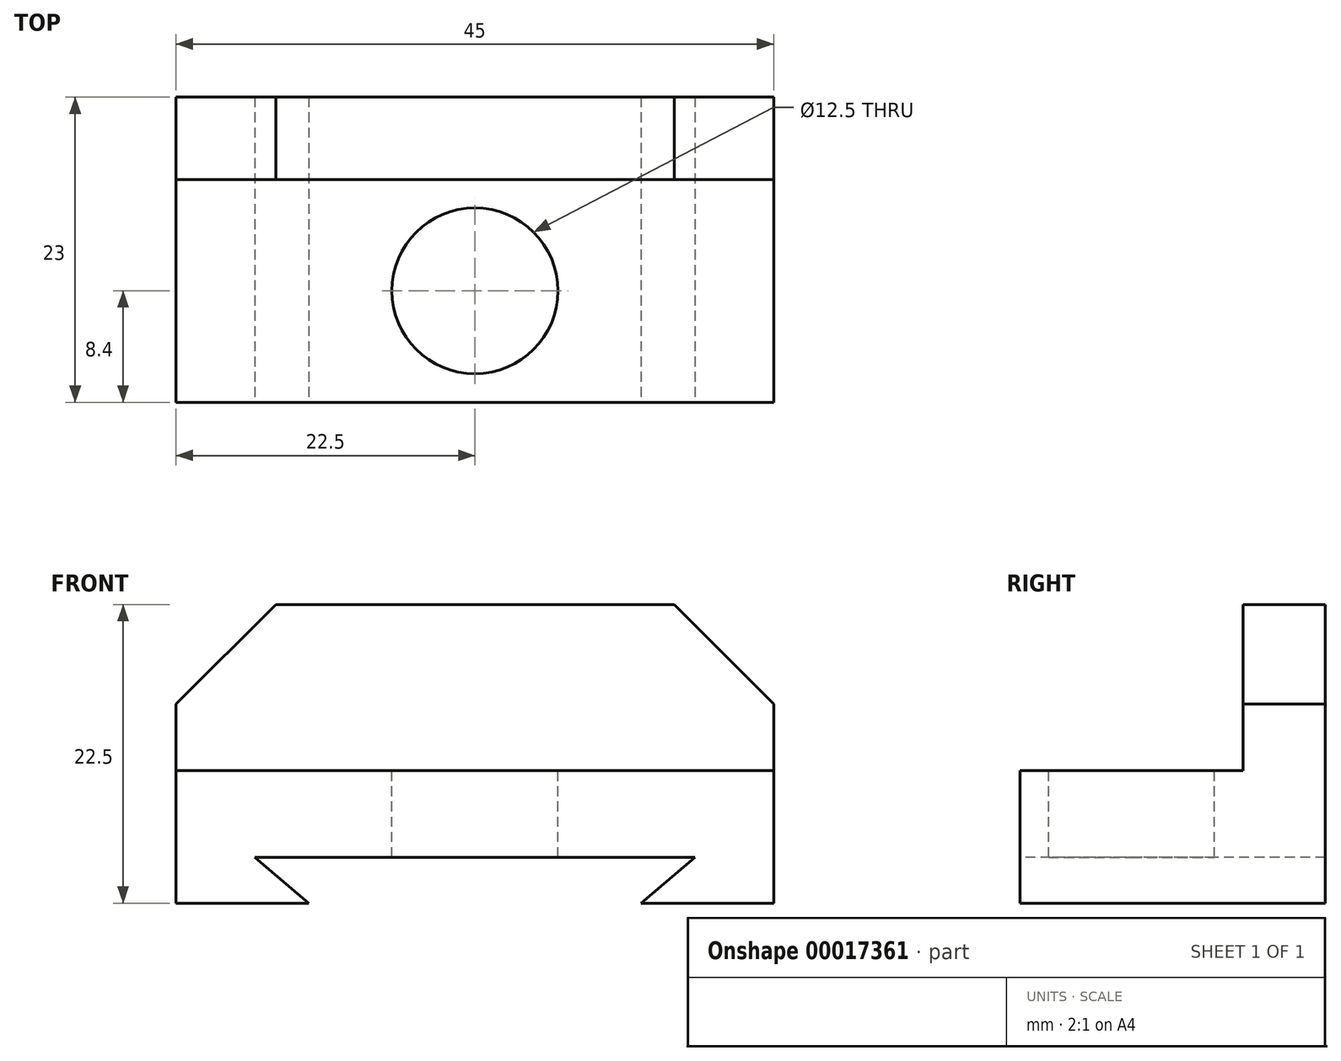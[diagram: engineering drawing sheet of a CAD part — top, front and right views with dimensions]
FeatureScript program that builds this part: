
annotation { "Feature Type Name" : "Feature", "Feature Type Description" : "" }
export const myFeature = defineFeature(function(context is Context, id is Id, definition is map)
    precondition{}
    {
        {
            var Q0;
            Q0=qCreatedBy(makeId("Front.planeOp"),FACE);
            var sketch = newSketch(context, id + "F0", { "sketchPlane" : qUnion([Q0])});
            skLineSegment(sketch, "E0", {"start": v(-24.57, -27) * mm, "end": v(-14.57, -27) * mm});
            skLineSegment(sketch, "E1", {"start": v(10.43, -27) * mm, "end": v(20.43, -27) * mm});
            skLineSegment(sketch, "E2", {"start": v(20.43, -27) * mm, "end": v(20.43, -17) * mm});
            skLineSegment(sketch, "E3", {"start": v(-24.57, -27) * mm, "end": v(-24.57, -17) * mm});
            skLineSegment(sketch, "E4", {"start": v(-24.57, -17) * mm, "end": v(20.43, -17) * mm});
            skLineSegment(sketch, "E5", {"start": v(-14.57, -27) * mm, "end": v(-18.64, -23.54) * mm});
            skLineSegment(sketch, "E6", {"start": v(10.43, -27) * mm, "end": v(14.5, -23.54) * mm});
            skLineSegment(sketch, "E7", {"start": v(14.5, -23.54) * mm, "end": v(-18.64, -23.54) * mm});
            skSolve(sketch);
        }
        {
            var Q0;
            Q0=makeQuery(id+"F0.imprint","IMPRINT",FACE,{"disambiguationData":[TD([[makeQuery(id+"F0.imprint","IMPRINT",EDGE,{"derivedFrom":sQuery(id+"F0.wireOp",EDGE,"E0")}),1.0]])]});
            extrude(context, id + "F1", {"entities" : qUnion([Q0]), "oppositeDirection" : true, "depth" : 23 * mm});
        }
        {
            var Q0;
            Q0=makeQuery(id+"F1.opExtrude","SWEPT_FACE",FACE,{"disambiguationData":[OSD([sQuery(id+"F0.wireOp",EDGE,"E4")])]});
            var sketch = newSketch(context, id + "F2", { "sketchPlane" : qUnion([Q0])});
            skLineSegment(sketch, "E8.bottom", {"start": v(-24.57, 23) * mm, "end": v(20.43, 23) * mm});
            skLineSegment(sketch, "E8.top", {"start": v(-24.57, 16.8) * mm, "end": v(20.43, 16.8) * mm});
            skLineSegment(sketch, "E8.left", {"start": v(-24.57, 23) * mm, "end": v(-24.57, 16.8) * mm});
            skLineSegment(sketch, "E8.right", {"start": v(20.43, 23) * mm, "end": v(20.43, 16.8) * mm});
            skSolve(sketch);
        }
        {
            var Q0;
            Q0=makeQuery(id+"F2.imprint","IMPRINT",FACE,{"disambiguationData":[TD([[makeQuery(id+"F2.imprint","IMPRINT",EDGE,{"derivedFrom":sQuery(id+"F2.wireOp",EDGE,"E8.bottom")}),-1.0]])]});
            extrude(context, id + "F3", {"entities" : qUnion([Q0]), "operationType" : NewBodyOperationType.ADD, "depth" : 12.5 * mm});
        }
        {
            var Q0;
            Q0=makeQuery(id+"F3.opExtrude","SWEPT_FACE",FACE,{"disambiguationData":[OSD([sQuery(id+"F2.wireOp",EDGE,"E8.top")])]});
            var sketch = newSketch(context, id + "F4", { "sketchPlane" : qUnion([Q0])});
            skLineSegment(sketch, "E9", {"start": v(-24.57, -17) * mm, "end": v(-24.57, -12) * mm});
            skLineSegment(sketch, "E10", {"start": v(20.43, -17) * mm, "end": v(20.43, -12) * mm});
            skLineSegment(sketch, "E11", {"start": v(-17.07, -4.5) * mm, "end": v(12.93, -4.5) * mm});
            skLineSegment(sketch, "E12", {"start": v(-17.07, -4.5) * mm, "end": v(-24.57, -12) * mm});
            skLineSegment(sketch, "E13", {"start": v(12.93, -4.5) * mm, "end": v(20.43, -12) * mm});
            skLineSegment(sketch, "E14", {"start": v(20.43, -12) * mm, "end": v(20.43, -4.5) * mm});
            skLineSegment(sketch, "E15", {"start": v(20.43, -4.5) * mm, "end": v(12.93, -4.5) * mm});
            skLineSegment(sketch, "E16", {"start": v(-24.57, -12) * mm, "end": v(-24.57, -4.5) * mm});
            skLineSegment(sketch, "E17", {"start": v(-24.57, -4.5) * mm, "end": v(-17.07, -4.5) * mm});
            skSolve(sketch);
        }
        {
            var Q0;
            Q0=makeQuery(id+"F4.imprint","IMPRINT",FACE,{"disambiguationData":[TD([[makeQuery(id+"F4.imprint","IMPRINT",EDGE,{"derivedFrom":sQuery(id+"F4.wireOp",EDGE,"E13")}),1.0]])]});
            extrude(context, id + "F5", {"entities" : qUnion([Q0]), "operationType" : NewBodyOperationType.REMOVE, "oppositeDirection" : true, "depth" : 25 * mm});
        }
        {
            var Q0;
            Q0=makeQuery(id+"F4.imprint","IMPRINT",FACE,{"disambiguationData":[TD([[makeQuery(id+"F4.imprint","IMPRINT",EDGE,{"derivedFrom":sQuery(id+"F4.wireOp",EDGE,"E12")}),-1.0]])]});
            extrude(context, id + "F6", {"entities" : qUnion([Q0]), "operationType" : NewBodyOperationType.REMOVE, "oppositeDirection" : true, "depth" : 25 * mm});
        }
        {
            var Q0;
            Q0=makeQuery(id+"F1.opExtrude","SWEPT_FACE",FACE,{"disambiguationData":[OSD([sQuery(id+"F0.wireOp",EDGE,"E4")])]});
            var sketch = newSketch(context, id + "F7", { "sketchPlane" : qUnion([Q0])});
            skCircle(sketch, "E18", {"center": v(-2.07, 8.4) * mm, "radius": 6.25 * mm});
            skSolve(sketch);
        }
        {
            var Q0;
            Q0=makeQuery(id+"F7.imprint","IMPRINT",FACE,{"disambiguationData":[TD([[makeQuery(id+"F7.imprint","IMPRINT",EDGE,{"derivedFrom":sQuery(id+"F7.wireOp",EDGE,"E18")}),1.0]])]});
            extrude(context, id + "F8", {"entities" : qUnion([Q0]), "operationType" : NewBodyOperationType.REMOVE, "oppositeDirection" : true, "depth" : 25 * mm});
        }
    });
